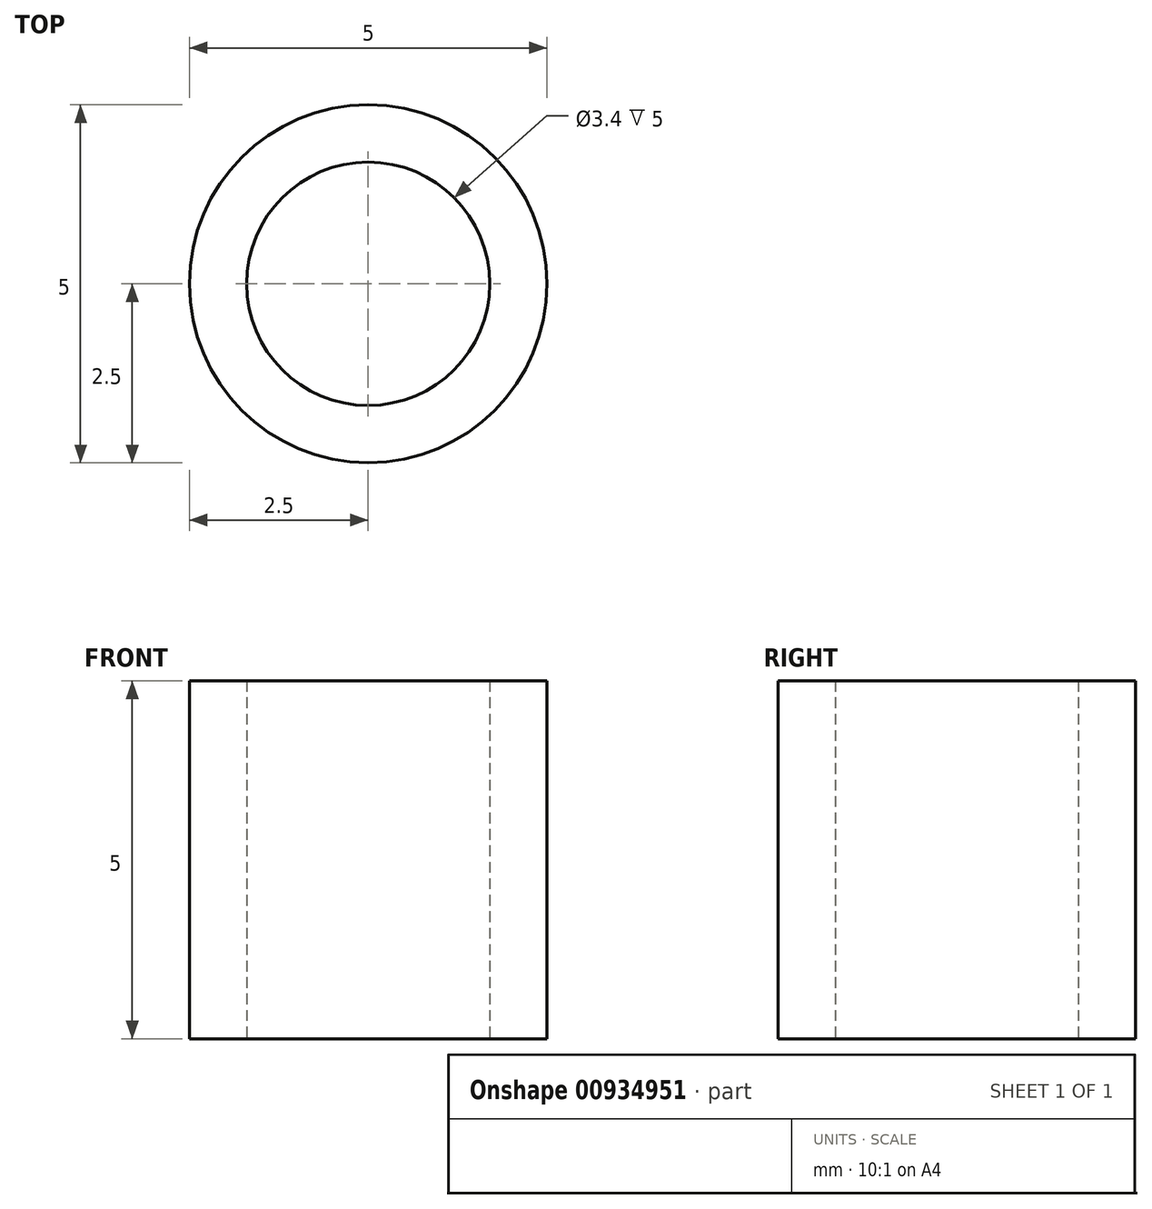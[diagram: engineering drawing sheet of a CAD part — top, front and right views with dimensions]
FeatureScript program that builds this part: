
annotation { "Feature Type Name" : "Feature", "Feature Type Description" : "" }
export const myFeature = defineFeature(function(context is Context, id is Id, definition is map)
    precondition{}
    {
        {
            var Q0;
            Q0=qCreatedBy(makeId("Top.planeOp"),FACE);
            var sketch = newSketch(context, id + "F0", { "sketchPlane" : qUnion([Q0])});
            skCircle(sketch, "E0", {"center": v(0, 0) * mm, "radius": 1.7 * mm});
            skCircle(sketch, "E1", {"center": v(0, 0) * mm, "radius": 2.5 * mm});
            skSolve(sketch);
        }
        {
            var Q0;
            Q0=makeQuery(id+"F0.imprint","IMPRINT",FACE,{"disambiguationData":[TD([[makeQuery(id+"F0.imprint","IMPRINT",EDGE,{"derivedFrom":sQuery(id+"F0.wireOp",EDGE,"E0")}),-1.0]])]});
            extrude(context, id + "F1", {"entities" : qUnion([Q0]), "depth" : 5 * mm, "offsetDistance" : 25 * mm});
        }
    });
